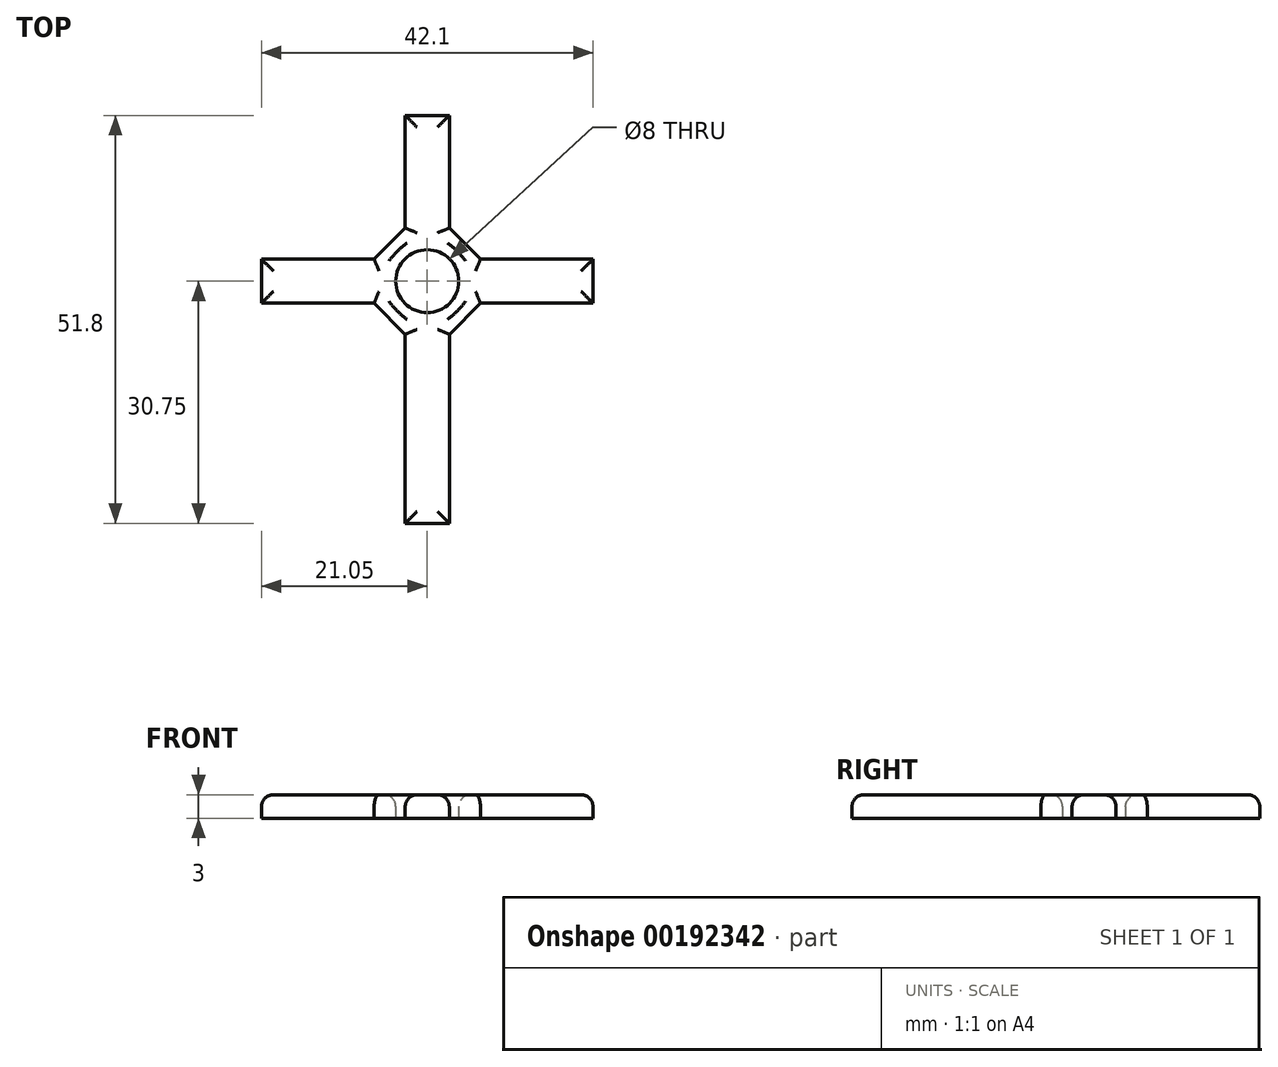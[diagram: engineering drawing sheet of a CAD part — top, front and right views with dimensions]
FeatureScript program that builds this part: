
annotation { "Feature Type Name" : "Feature", "Feature Type Description" : "" }
export const myFeature = defineFeature(function(context is Context, id is Id, definition is map)
    precondition{}
    {
        {
            var Q0;
            Q0=qCreatedBy(makeId("Top.planeOp"),FACE);
            var sketch = newSketch(context, id + "F0", { "sketchPlane" : qUnion([Q0])});
            skLineSegment(sketch, "E0.1", {"start": v(-2.8, -6.75) * mm, "end": v(-6.75, -2.8) * mm});
            skLineSegment(sketch, "E0.3", {"start": v(-6.75, 2.8) * mm, "end": v(-2.8, 6.75) * mm});
            skLineSegment(sketch, "E0.5", {"start": v(2.8, 6.75) * mm, "end": v(6.75, 2.8) * mm});
            skLineSegment(sketch, "E0.7", {"start": v(6.75, -2.8) * mm, "end": v(2.8, -6.75) * mm});
            skPoint(sketch, "E0.0.midPoint", {"position": v(0, -6.75) * mm});
            skLineSegment(sketch, "E1", {"start": v(-6.75, 2.8) * mm, "end": v(-21.05, 2.8) * mm});
            skLineSegment(sketch, "E2", {"start": v(-6.75, -2.8) * mm, "end": v(-21.05, -2.8) * mm});
            skLineSegment(sketch, "E3", {"start": v(-21.05, 2.8) * mm, "end": v(-21.05, -2.8) * mm});
            skLineSegment(sketch, "E4", {"start": v(-2.8, 6.75) * mm, "end": v(-2.8, 21.05) * mm});
            skLineSegment(sketch, "E5", {"start": v(-2.8, 21.05) * mm, "end": v(2.8, 21.05) * mm});
            skLineSegment(sketch, "E6", {"start": v(2.8, 21.05) * mm, "end": v(2.8, 6.75) * mm});
            skLineSegment(sketch, "E7", {"start": v(6.75, 2.8) * mm, "end": v(21.05, 2.8) * mm});
            skLineSegment(sketch, "E8", {"start": v(6.75, -2.8) * mm, "end": v(21.05, -2.8) * mm});
            skLineSegment(sketch, "E9", {"start": v(21.05, 2.8) * mm, "end": v(21.05, -2.8) * mm});
            skLineSegment(sketch, "E10", {"start": v(-2.8, -6.75) * mm, "end": v(-2.8, -30.75) * mm});
            skLineSegment(sketch, "E11", {"start": v(2.8, -6.75) * mm, "end": v(2.8, -30.75) * mm});
            skLineSegment(sketch, "E12", {"start": v(2.8, -30.75) * mm, "end": v(-2.8, -30.75) * mm});
            skCircle(sketch, "E13", {"center": v(0, 0) * mm, "radius": 4 * mm});
            skSolve(sketch);
        }
        {
            var Q0;
            Q0=makeQuery(id+"F0.imprint","IMPRINT",FACE,{"disambiguationData":[TD([[makeQuery(id+"F0.imprint","IMPRINT",EDGE,{"derivedFrom":sQuery(id+"F0.wireOp",EDGE,"E0.1")}),-1.0]])]});
            extrude(context, id + "F1", {"entities" : qUnion([Q0]), "depth" : 3 * mm});
        }
        {
            var Q0;
            Q0=makeQuery(id+"F1.opExtrude","CAP_EDGE",EDGE,{"disambiguationData":[OSD([sQuery(id+"F0.wireOp",EDGE,"E1")])],"isStart":false});
            var Q1;
            Q1=makeQuery(id+"F1.opExtrude","CAP_EDGE",EDGE,{"disambiguationData":[OSD([sQuery(id+"F0.wireOp",EDGE,"E3")])],"isStart":false});
            var Q2;
            Q2=makeQuery(id+"F1.opExtrude","CAP_EDGE",EDGE,{"disambiguationData":[OSD([sQuery(id+"F0.wireOp",EDGE,"E12")])],"isStart":false});
            var Q3;
            Q3=makeQuery(id+"F1.opExtrude","CAP_EDGE",EDGE,{"disambiguationData":[OSD([sQuery(id+"F0.wireOp",EDGE,"E11")])],"isStart":false});
            var Q4;
            Q4=makeQuery(id+"F1.opExtrude","CAP_EDGE",EDGE,{"disambiguationData":[OSD([sQuery(id+"F0.wireOp",EDGE,"E0.7")])],"isStart":false});
            var Q5;
            Q5=makeQuery(id+"F1.opExtrude","CAP_EDGE",EDGE,{"disambiguationData":[OSD([sQuery(id+"F0.wireOp",EDGE,"E8")])],"isStart":false});
            var Q6;
            Q6=makeQuery(id+"F1.opExtrude","CAP_EDGE",EDGE,{"disambiguationData":[OSD([sQuery(id+"F0.wireOp",EDGE,"E2")])],"isStart":false});
            var Q7;
            Q7=makeQuery(id+"F1.opExtrude","CAP_EDGE",EDGE,{"disambiguationData":[OSD([sQuery(id+"F0.wireOp",EDGE,"E10")])],"isStart":false});
            var Q8;
            Q8=makeQuery(id+"F1.opExtrude","CAP_EDGE",EDGE,{"disambiguationData":[OSD([sQuery(id+"F0.wireOp",EDGE,"E0.1")])],"isStart":false});
            var Q9;
            Q9=makeQuery(id+"F1.opExtrude","CAP_EDGE",EDGE,{"disambiguationData":[OSD([sQuery(id+"F0.wireOp",EDGE,"E0.3")])],"isStart":false});
            var Q10;
            Q10=makeQuery(id+"F1.opExtrude","CAP_EDGE",EDGE,{"disambiguationData":[OSD([sQuery(id+"F0.wireOp",EDGE,"E4")])],"isStart":false});
            var Q11;
            Q11=makeQuery(id+"F1.opExtrude","CAP_FACE",FACE,{"disambiguationData":[OSD([sQuery(id+"F0.wireOp",EDGE,"E0.1"),sQuery(id+"F0.wireOp",EDGE,"E0.3"),sQuery(id+"F0.wireOp",EDGE,"E0.5"),sQuery(id+"F0.wireOp",EDGE,"E0.7"),sQuery(id+"F0.wireOp",EDGE,"E1"),sQuery(id+"F0.wireOp",EDGE,"E2"),sQuery(id+"F0.wireOp",EDGE,"E3"),sQuery(id+"F0.wireOp",EDGE,"E4"),sQuery(id+"F0.wireOp",EDGE,"E5"),sQuery(id+"F0.wireOp",EDGE,"E6"),sQuery(id+"F0.wireOp",EDGE,"E7"),sQuery(id+"F0.wireOp",EDGE,"E8"),sQuery(id+"F0.wireOp",EDGE,"E9"),sQuery(id+"F0.wireOp",EDGE,"E10"),sQuery(id+"F0.wireOp",EDGE,"E11"),sQuery(id+"F0.wireOp",EDGE,"E12"),sQuery(id+"F0.wireOp",EDGE,"E13")])],"isStart":false});
            fillet(context, id + "F2", {"entities" : qUnion([Q0, Q1, Q2, Q3, Q4, Q5, Q6, Q7, Q8, Q9, Q10, Q11]), "radius" : 1.5 * mm, "allowEdgeOverflow" : false});
        }
    });
